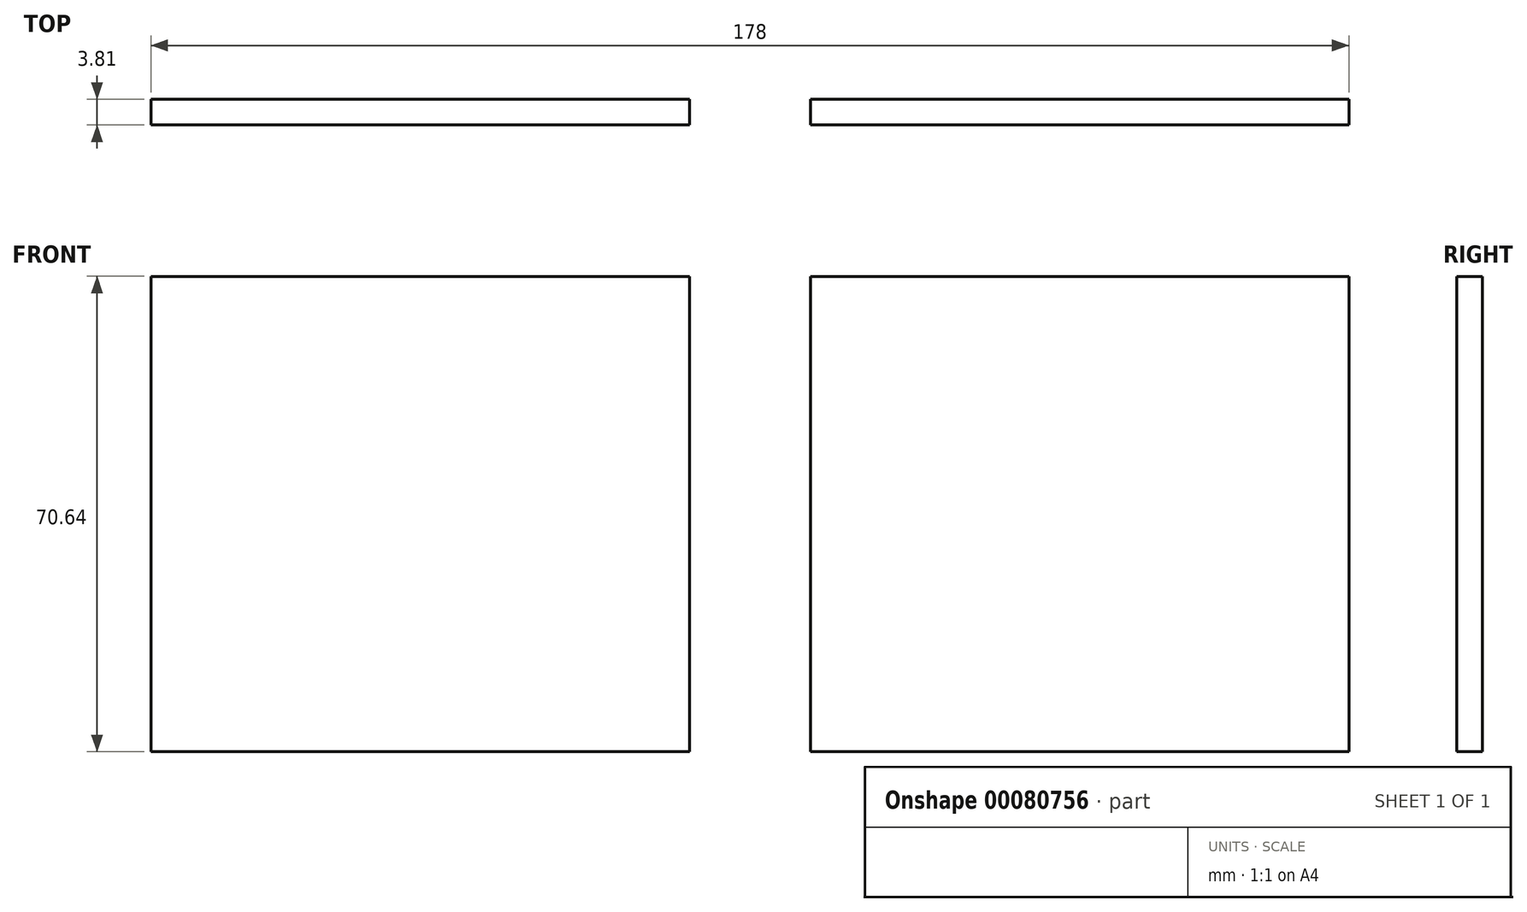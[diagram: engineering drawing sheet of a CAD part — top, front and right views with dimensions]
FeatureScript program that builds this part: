
annotation { "Feature Type Name" : "Feature", "Feature Type Description" : "" }
export const myFeature = defineFeature(function(context is Context, id is Id, definition is map)
    precondition{}
    {
        {
            var Q0;
            Q0=qCreatedBy(makeId("Front.planeOp"),FACE);
            var sketch = newSketch(context, id + "F0", { "sketchPlane" : qUnion([Q0])});
            skLineSegment(sketch, "E0.bottom", {"start": v(89, 35.32) * mm, "end": v(-89, 35.32) * mm});
            skLineSegment(sketch, "E0.top", {"start": v(89, -35.32) * mm, "end": v(-89, -35.32) * mm});
            skLineSegment(sketch, "E0.left", {"start": v(89, 35.32) * mm, "end": v(89, -35.32) * mm});
            skLineSegment(sketch, "E0.right", {"start": v(-89, 35.32) * mm, "end": v(-89, -35.32) * mm});
            skPoint(sketch, "E0.middle", {"position": v(0, 0) * mm});
            skLineSegment(sketch, "E1.bottom", {"start": v(9, 35.32) * mm, "end": v(-9, 35.32) * mm});
            skLineSegment(sketch, "E1.top", {"start": v(9, -35.32) * mm, "end": v(-9, -35.32) * mm});
            skLineSegment(sketch, "E1.left", {"start": v(9, 35.32) * mm, "end": v(9, -35.32) * mm});
            skLineSegment(sketch, "E1.right", {"start": v(-9, 35.32) * mm, "end": v(-9, -35.32) * mm});
            skLineSegment(sketch, "E2", {"start": v(-9, 14.68) * mm, "end": v(9, 14.68) * mm});
            skSolve(sketch);
        }
        {
            var Q0;
            {var subQ0=sQuery(id+"F0.wireOp",EDGE,"E0.right");Q0=makeQuery(id+"F0.imprint","IMPRINT",FACE,{"disambiguationData":[TD([[makeQuery(id+"F0.imprint","IMPRINT",EDGE,{"derivedFrom":subQ0}),1.0]])]});}
            var Q1;
            {var subQ0=sQuery(id+"F0.wireOp",EDGE,"E0.left");Q1=makeQuery(id+"F0.imprint","IMPRINT",FACE,{"disambiguationData":[TD([[makeQuery(id+"F0.imprint","IMPRINT",EDGE,{"derivedFrom":subQ0}),-1.0]])]});}
            var Q2;
            {var subQ0=sQuery(id+"F0.wireOp",EDGE,"E1.bottom");Q2=makeQuery(id+"F0.imprint","IMPRINT",FACE,{"disambiguationData":[TD([[makeQuery(id+"F0.imprint","IMPRINT",EDGE,{"derivedFrom":subQ0}),1.0]])]});}
            extrude(context, id + "F1", {"entities" : qUnion([Q0, Q1, Q2]), "depth" : 3.8 * mm});
        }
    });
